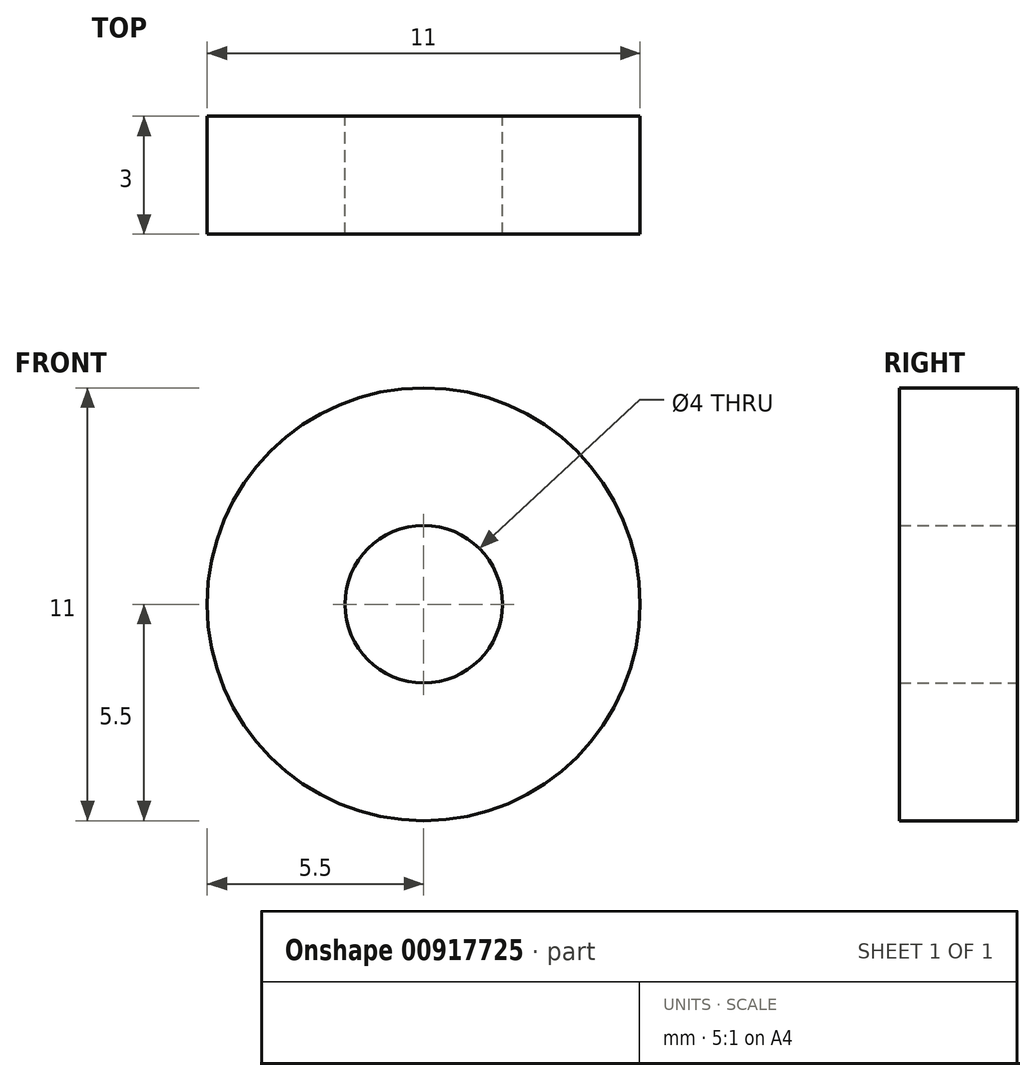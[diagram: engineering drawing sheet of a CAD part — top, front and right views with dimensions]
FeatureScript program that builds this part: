
annotation { "Feature Type Name" : "Feature", "Feature Type Description" : "" }
export const myFeature = defineFeature(function(context is Context, id is Id, definition is map)
    precondition{}
    {
        {
            var Q0;
            Q0=qCreatedBy(makeId("Front.planeOp"),FACE);
            var sketch = newSketch(context, id + "F0", { "sketchPlane" : qUnion([Q0])});
            skCircle(sketch, "E0", {"center": v(0, 0) * mm, "radius": 2 * mm});
            skCircle(sketch, "E1", {"center": v(0, 0) * mm, "radius": 5.5 * mm});
            skSolve(sketch);
        }
        {
            var Q0;
            Q0=makeQuery(id+"F0.imprint","IMPRINT",FACE,{"disambiguationData":[TD([[makeQuery(id+"F0.imprint","IMPRINT",EDGE,{"derivedFrom":sQuery(id+"F0.wireOp",EDGE,"E0")}),-1.0]])]});
            extrude(context, id + "F1", {"entities" : qUnion([Q0]), "depth" : 3 * mm, "offsetDistance" : 25 * mm, "symmetric" : true});
        }
    });
